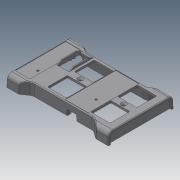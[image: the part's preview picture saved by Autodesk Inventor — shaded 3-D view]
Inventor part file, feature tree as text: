
AUTODESK INVENTOR PART (.ipt)
format: ipt  version: 2020.3 (Build 243373000, 373)  size: 683,008 bytes
history: native  units: in
note: dims shown in document units (in); Inventor stores cm internally (conversion verified against a paired STEP export)
features: chamfer x1
ambient origin geometry x8: Origin, YZ Plane, XZ Plane, XY Plane, X Axis, Y Axis, Z Axis, Center Point
bodies: Solid1 (feature_tree)
feature tree (1):
  chamfer  "Chamfer6"  [1 undecoded]
note: 1 required parameter value undecoded (feature->parameter linkage not recoverable at this tier; creation-order binding heuristic only, values carry confidence <= 0.55)
